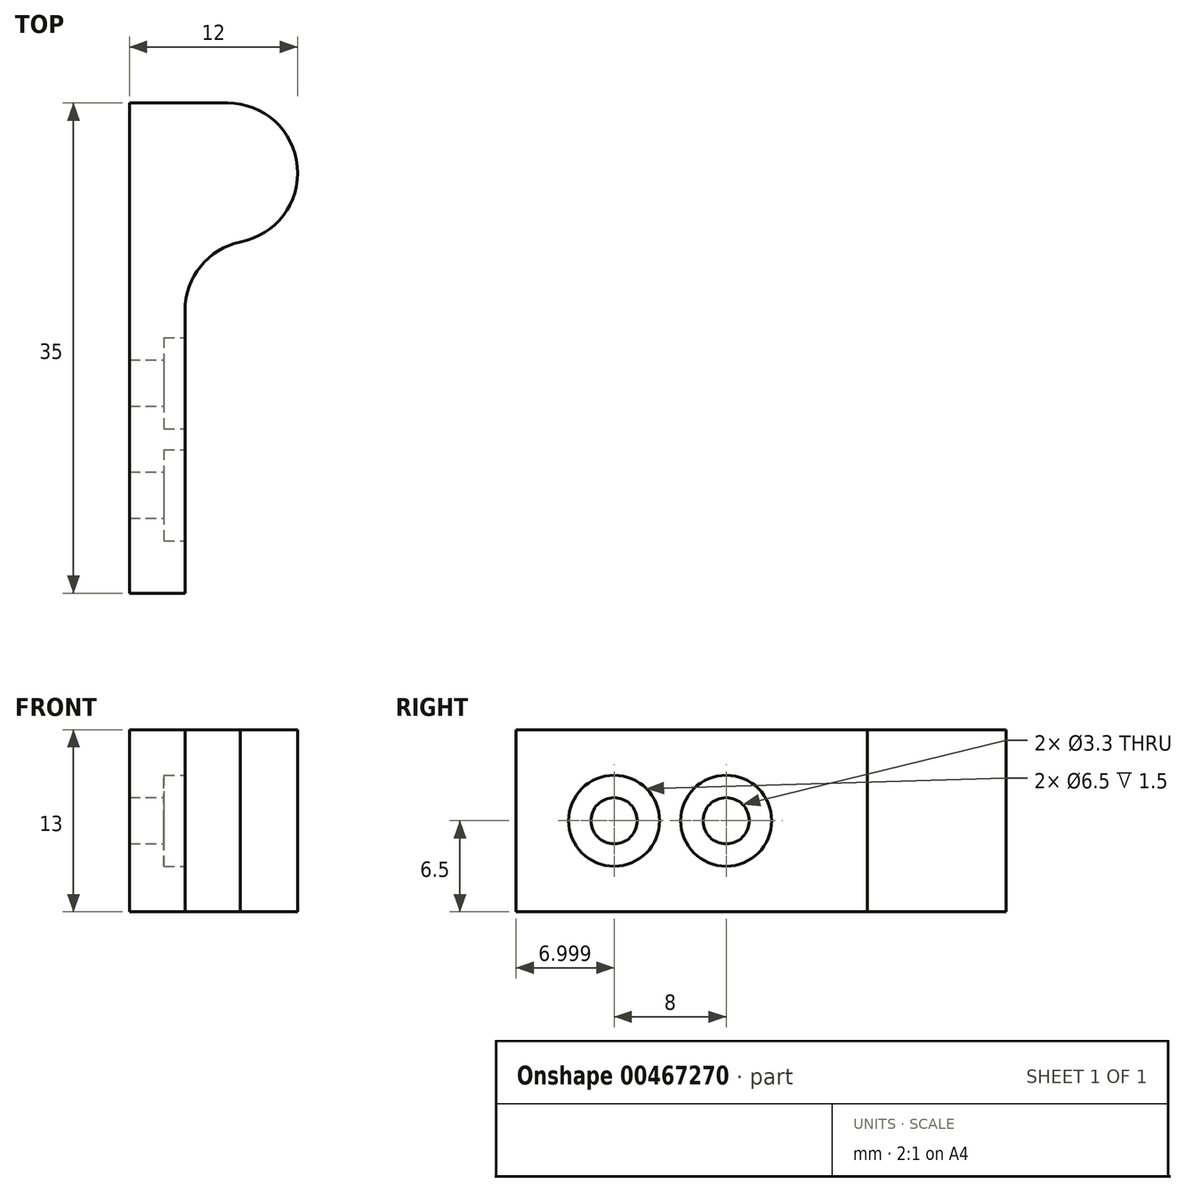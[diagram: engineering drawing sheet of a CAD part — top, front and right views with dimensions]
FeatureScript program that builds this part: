
annotation { "Feature Type Name" : "Feature", "Feature Type Description" : "" }
export const myFeature = defineFeature(function(context is Context, id is Id, definition is map)
    precondition{}
    {
        {
            var Q0;
            Q0=qCreatedBy(makeId("Top.planeOp"),FACE);
            var sketch = newSketch(context, id + "F0", { "sketchPlane" : qUnion([Q0])});
            skLineSegment(sketch, "E0", {"start": v(-0.82, 5.85) * mm, "end": v(6.18, 5.85) * mm});
            skArc(sketch, "E1", {"start": v(6.18, 5.85) * mm, "mid": v(11.16, 1.3) * mm, "end": v(7.1, -4.07) * mm});
            skLineSegment(sketch, "E2", {"start": v(-0.82, 5.85) * mm, "end": v(-0.82, -29.15) * mm});
            skLineSegment(sketch, "E3", {"start": v(-0.82, -29.15) * mm, "end": v(3.14, -29.15) * mm});
            skLineSegment(sketch, "E4", {"start": v(7.1, -4.07) * mm, "end": v(3.14, -4.07) * mm});
            skPoint(sketch, "E4.endSnap0", {"position": v(3.14, -29.15) * mm});
            skLineSegment(sketch, "E5", {"start": v(3.14, -4.07) * mm, "end": v(3.14, -29.15) * mm});
            skCircle(sketch, "E6", {"center": v(6.18, 0.85) * mm, "radius": 1.25 * mm, "construction": true});
            skSolve(sketch);
        }
        {
            var Q0;
            Q0=qSketchRegion(id+"F0",true);
            extrude(context, id + "F1", {"entities" : qUnion([Q0]), "depth" : 13 * mm});
        }
        {
            var Q0;
            Q0=makeQuery(id+"F1.opExtrude","SWEPT_EDGE",EDGE,{"disambiguationData":[OSD([sQuery(id+"F0.wireOp",EDGE,"E4"),sQuery(id+"F0.wireOp",EDGE,"E5")])]});
            fillet(context, id + "F2", {"entities" : qUnion([Q0]), "radius" : 5 * mm, "tangentPropagation" : true, "allowEdgeOverflow" : false});
        }
        {
            var Q0;
            Q0=makeQuery(id+"F1.opExtrude","SWEPT_FACE",FACE,{"disambiguationData":[OSD([sQuery(id+"F0.wireOp",EDGE,"E5")])]});
            var sketch = newSketch(context, id + "F3", { "sketchPlane" : qUnion([Q0])});
            skPoint(sketch, "E7", {"position": v(-22.15, 6.5) * mm});
            skPoint(sketch, "E7.positionSnap0", {"position": v(-29.15, 6.5) * mm});
            skPoint(sketch, "E8", {"position": v(-14.15, 6.5) * mm});
            skSolve(sketch);
        }
        {
            var Q0;
            Q0=sQuery(id+"F3.wireOp",VERTEX,"E7");
            var Q1;
            Q1=sQuery(id+"F3.wireOp",VERTEX,"E8");
            var Q2;
            Q2=makeQuery(id+"F1.opExtrude","SWEPT_BODY",BODY,{"disambiguationData":[OSD([sQuery(id+"F0.wireOp",EDGE,"E0"),sQuery(id+"F0.wireOp",EDGE,"E1"),sQuery(id+"F0.wireOp",EDGE,"E2"),sQuery(id+"F0.wireOp",EDGE,"E3"),sQuery(id+"F0.wireOp",EDGE,"E4"),sQuery(id+"F0.wireOp",EDGE,"E5"),sQuery(id+"F0.wireOp",EDGE,"E6")])]});
            hole(context, id + "F4", {"style" : HoleStyle.C_BORE, "endStyle" : HoleEndStyle.THROUGH, "holeDiameter" : 3.3 * mm, "cBoreDiameter" : 6.5 * mm, "cBoreDepth" : 1.5 * mm, "isTappedThrough" : true, "tappedDepth" : 12 * mm, "tapClearance" : 3, "locations" : qUnion([Q0, Q1]), "scope" : qUnion([Q2])});
        }
    });
